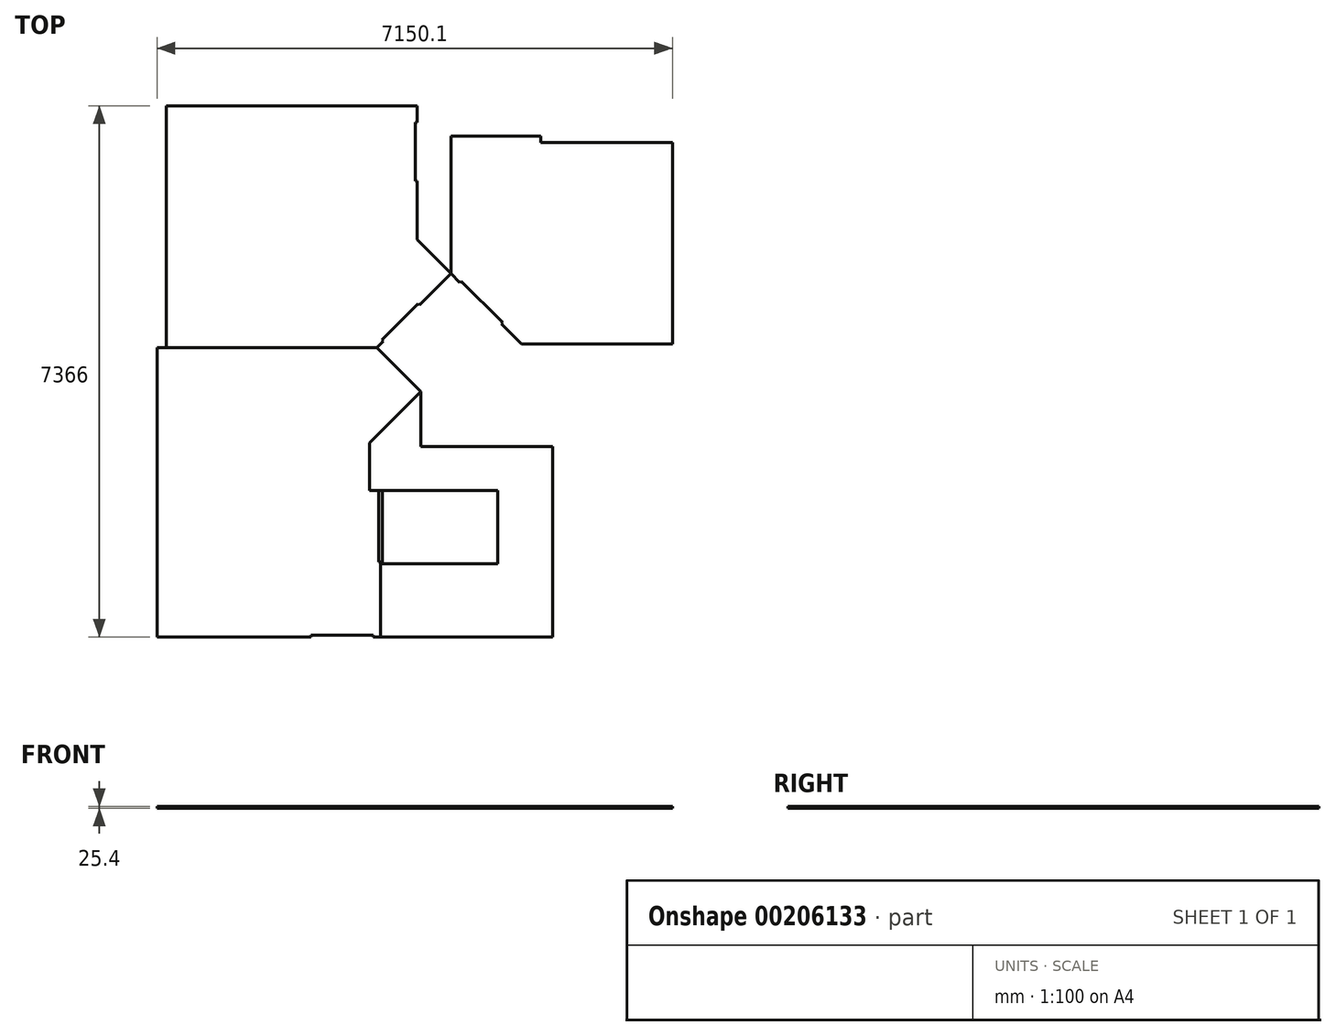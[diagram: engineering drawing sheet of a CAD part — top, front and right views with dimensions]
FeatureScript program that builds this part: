
annotation { "Feature Type Name" : "Feature", "Feature Type Description" : "" }
export const myFeature = defineFeature(function(context is Context, id is Id, definition is map)
    precondition{}
    {
        {
            var Q0;
            Q0=qCreatedBy(makeId("Top.planeOp"),FACE);
            var sketch = newSketch(context, id + "F0", { "sketchPlane" : qUnion([Q0])});
            skLineSegment(sketch, "E0", {"start": v(-1524, 2006.6) * mm, "end": v(-1524, -2006.6) * mm});
            skLineSegment(sketch, "E1", {"start": v(-1524, -2006.6) * mm, "end": v(609.6, -2006.6) * mm});
            skLineSegment(sketch, "E2", {"start": v(609.6, -1981.2) * mm, "end": v(609.6, -2032) * mm});
            skLineSegment(sketch, "E3", {"start": v(1473.2, -1981.2) * mm, "end": v(1473.2, -2032) * mm});
            skLineSegment(sketch, "E4", {"start": v(609.6, -1981.2) * mm, "end": v(1473.2, -1981.2) * mm});
            skLineSegment(sketch, "E5", {"start": v(1473.2, -2006.6) * mm, "end": v(1574.8, -2006.6) * mm});
            skLineSegment(sketch, "E6", {"start": v(1574.8, -2006.6) * mm, "end": v(1574.8, -965.2) * mm});
            skLineSegment(sketch, "E7", {"start": v(-1524, 2006.6) * mm, "end": v(1524, 2006.6) * mm});
            skLineSegment(sketch, "E8", {"start": v(1524, 2006.6) * mm, "end": v(2134.66, 1395.94) * mm});
            skLineSegment(sketch, "E9", {"start": v(2134.66, 1395.94) * mm, "end": v(1422.4, 683.69) * mm});
            skLineSegment(sketch, "E10", {"start": v(1422.4, 683.69) * mm, "end": v(1422.4, 25.4) * mm});
            skLineSegment(sketch, "E11", {"start": v(1422.4, 25.4) * mm, "end": v(3200.4, 25.4) * mm});
            skLineSegment(sketch, "E12", {"start": v(2134.66, 1395.94) * mm, "end": v(2134.66, 635) * mm});
            skLineSegment(sketch, "E13", {"start": v(3200.4, 25.4) * mm, "end": v(3200.4, -990.6) * mm});
            skLineSegment(sketch, "E14", {"start": v(3200.4, -990.6) * mm, "end": v(2692.4, -990.6) * mm});
            skLineSegment(sketch, "E15", {"start": v(2692.4, -990.6) * mm, "end": v(2692.4, -2006.6) * mm, "construction": true});
            skLineSegment(sketch, "E16", {"start": v(2692.4, -2006.6) * mm, "end": v(1574.8, -2006.6) * mm});
            skLineSegment(sketch, "E17", {"start": v(1549.4, -965.2) * mm, "end": v(1600.2, -965.2) * mm});
            skLineSegment(sketch, "E18", {"start": v(1600.2, -965.2) * mm, "end": v(1600.2, 25.4) * mm});
            skLineSegment(sketch, "E19", {"start": v(1549.4, -965.2) * mm, "end": v(1549.4, 25.4) * mm});
            skLineSegment(sketch, "E20", {"start": v(1422.4, 25.4) * mm, "end": v(1549.4, 25.4) * mm});
            skLineSegment(sketch, "E21", {"start": v(2692.4, -2006.6) * mm, "end": v(3962.4, -2006.6) * mm});
            skLineSegment(sketch, "E22", {"start": v(3962.4, -2006.6) * mm, "end": v(3962.4, 635) * mm});
            skLineSegment(sketch, "E23", {"start": v(3962.4, 635) * mm, "end": v(2134.66, 635) * mm});
            skLineSegment(sketch, "E24", {"start": v(2692.4, -990.6) * mm, "end": v(1574.8, -990.6) * mm});
            skLineSegment(sketch, "E25", {"start": v(0, 0) * mm, "end": v(-1524, 0) * mm, "construction": true});
            skPoint(sketch, "E25.endSnap0", {"position": v(-1524, 0) * mm});
            skLineSegment(sketch, "E26", {"start": v(1524, 2006.6) * mm, "end": v(1613.8, 2096.4) * mm});
            skLineSegment(sketch, "E27", {"start": v(1595.84, 2114.36) * mm, "end": v(1631.76, 2078.44) * mm});
            skLineSegment(sketch, "E28", {"start": v(1595.84, 2114.36) * mm, "end": v(2098.74, 2617.26) * mm});
            skLineSegment(sketch, "E29", {"start": v(2098.74, 2617.26) * mm, "end": v(2134.66, 2581.34) * mm});
            skLineSegment(sketch, "E30", {"start": v(2134.66, 2581.34) * mm, "end": v(1631.76, 2078.44) * mm});
            skLineSegment(sketch, "E31", {"start": v(2116.7, 2599.3) * mm, "end": v(2552.7, 3035.3) * mm});
            skLineSegment(sketch, "E32", {"start": v(-1397, 2006.6) * mm, "end": v(-1397, 5359.4) * mm});
            skLineSegment(sketch, "E33", {"start": v(-1397, 5359.4) * mm, "end": v(2082.8, 5359.4) * mm});
            skLineSegment(sketch, "E34", {"start": v(2082.8, 5359.4) * mm, "end": v(2082.8, 5130.8) * mm});
            skLineSegment(sketch, "E35", {"start": v(2057.4, 5130.8) * mm, "end": v(2108.2, 5130.8) * mm});
            skLineSegment(sketch, "E36", {"start": v(2057.4, 5130.8) * mm, "end": v(2057.4, 4318) * mm});
            skLineSegment(sketch, "E37", {"start": v(2057.4, 4318) * mm, "end": v(2108.2, 4318) * mm});
            skLineSegment(sketch, "E38", {"start": v(2108.2, 4318) * mm, "end": v(2108.2, 5130.8) * mm});
            skLineSegment(sketch, "E39", {"start": v(2082.8, 4318) * mm, "end": v(2082.8, 3505.2) * mm});
            skLineSegment(sketch, "E40", {"start": v(2082.8, 3505.2) * mm, "end": v(2552.7, 3035.3) * mm});
            skLineSegment(sketch, "E41", {"start": v(2082.8, 5359.4) * mm, "end": v(2552.7, 5359.4) * mm});
            skLineSegment(sketch, "E42", {"start": v(2552.7, 5359.4) * mm, "end": v(2552.7, 3035.3) * mm});
            skLineSegment(sketch, "E43", {"start": v(2552.7, 3035.3) * mm, "end": v(2678.42, 2909.58) * mm});
            skLineSegment(sketch, "E44", {"start": v(2696.38, 2927.54) * mm, "end": v(2660.46, 2891.62) * mm});
            skLineSegment(sketch, "E45", {"start": v(2696.38, 2927.54) * mm, "end": v(3271.12, 2352.8) * mm});
            skLineSegment(sketch, "E46", {"start": v(3235.2, 2316.88) * mm, "end": v(3271.12, 2352.8) * mm});
            skLineSegment(sketch, "E47", {"start": v(3235.2, 2316.88) * mm, "end": v(2660.46, 2891.62) * mm});
            skLineSegment(sketch, "E48", {"start": v(3253.16, 2334.84) * mm, "end": v(3530.6, 2057.4) * mm});
            skLineSegment(sketch, "E49", {"start": v(2552.7, 4940.3) * mm, "end": v(3797.3, 4940.3) * mm});
            skLineSegment(sketch, "E50", {"start": v(3797.3, 4940.3) * mm, "end": v(3797.3, 4851.4) * mm});
            skLineSegment(sketch, "E51", {"start": v(3797.3, 4851.4) * mm, "end": v(5626.1, 4851.4) * mm});
            skLineSegment(sketch, "E52", {"start": v(5626.1, 4851.4) * mm, "end": v(5626.1, 2057.4) * mm});
            skLineSegment(sketch, "E53", {"start": v(5626.1, 2057.4) * mm, "end": v(3530.6, 2057.4) * mm});
            skSolve(sketch);
        }
        {
            var Q0;
            Q0=makeQuery(id+"F0.imprint","IMPRINT",FACE,{"disambiguationData":[TD([[makeQuery(id+"F0.imprint","IMPRINT",EDGE,{"derivedFrom":sQuery(id+"F0.wireOp",EDGE,"E0")}),1.0]])]});
            extrude(context, id + "F1", {"entities" : qUnion([Q0]), "depth" : 25.4 * mm});
        }
        {
            var Q0;
            {var subQ0=sQuery(id+"F0.wireOp",EDGE,"E13");Q0=makeQuery(id+"F0.imprint","IMPRINT",FACE,{"disambiguationData":[TD([[makeQuery(id+"F0.imprint","IMPRINT",EDGE,{"derivedFrom":subQ0}),-1.0]])]});}
            extrude(context, id + "F2", {"entities" : qUnion([Q0]), "depth" : 25.4 * mm});
        }
        {
            var Q0;
            Q0=makeQuery(id+"F0.imprint","IMPRINT",FACE,{"disambiguationData":[TD([[makeQuery(id+"F0.imprint","IMPRINT",EDGE,{"derivedFrom":sQuery(id+"F0.wireOp",EDGE,"E9")}),1.0]])]});
            extrude(context, id + "F3", {"entities" : qUnion([Q0]), "depth" : 25.4 * mm});
        }
        {
            var Q0;
            {var subQ5=sQuery(id+"F0.wireOp",EDGE,"E26");Q0=makeQuery(id+"F0.imprint","IMPRINT",FACE,{"disambiguationData":[TD([[makeQuery(id+"F0.imprint","IMPRINT",EDGE,{"derivedFrom":subQ5}),1.0]])]});}
            extrude(context, id + "F4", {"entities" : qUnion([Q0]), "depth" : 25.4 * mm});
        }
        {
            var Q0;
            {var subQ3=sQuery(id+"F0.wireOp",EDGE,"E43");Q0=makeQuery(id+"F0.imprint","IMPRINT",FACE,{"disambiguationData":[TD([[makeQuery(id+"F0.imprint","IMPRINT",EDGE,{"derivedFrom":subQ3}),1.0]])]});}
            extrude(context, id + "F5", {"entities" : qUnion([Q0]), "depth" : 25.4 * mm});
        }
    });
